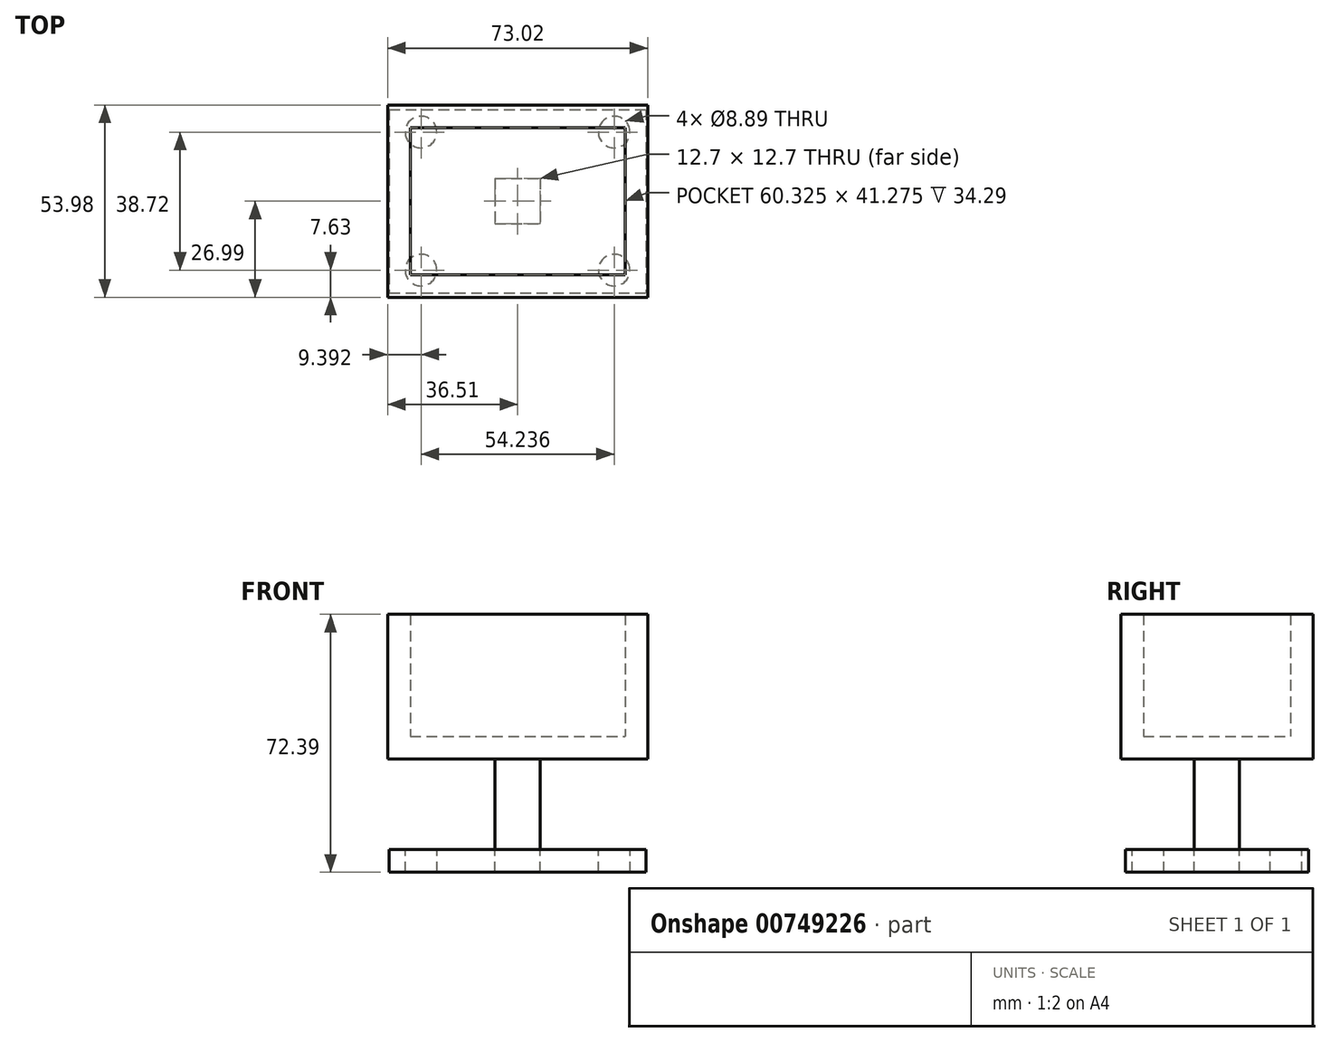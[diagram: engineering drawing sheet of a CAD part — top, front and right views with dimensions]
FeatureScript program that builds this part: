
annotation { "Feature Type Name" : "Feature", "Feature Type Description" : "" }
export const myFeature = defineFeature(function(context is Context, id is Id, definition is map)
    precondition{}
    {
        {
            var Q0;
            Q0=qCreatedBy(makeId("Top.planeOp"),FACE);
            var sketch = newSketch(context, id + "F0", { "sketchPlane" : qUnion([Q0])});
            skLineSegment(sketch, "E0.bottom", {"start": v(-30.16, -20.64) * mm, "end": v(30.16, -20.64) * mm});
            skLineSegment(sketch, "E0.top", {"start": v(-30.16, 20.64) * mm, "end": v(30.16, 20.64) * mm});
            skLineSegment(sketch, "E0.left", {"start": v(-30.16, -20.64) * mm, "end": v(-30.16, 20.64) * mm});
            skLineSegment(sketch, "E0.right", {"start": v(30.16, -20.64) * mm, "end": v(30.16, 20.64) * mm});
            skPoint(sketch, "E0.middle", {"position": v(0, 0) * mm});
            skSolve(sketch);
        }
        {
            var Q0;
            Q0=makeQuery(id+"F0.imprint","IMPRINT",FACE,{"disambiguationData":[TD([[makeQuery(id+"F0.imprint","IMPRINT",EDGE,{"derivedFrom":sQuery(id+"F0.wireOp",EDGE,"E0.bottom")}),1.0]])]});
            extrude(context, id + "F1", {"entities" : qUnion([Q0]), "depth" : 6.35 * mm});
        }
        {
            var Q0;
            Q0=makeQuery(id+"F1.opExtrude","CAP_FACE",FACE,{"disambiguationData":[OSD([sQuery(id+"F0.wireOp",EDGE,"E0.bottom"),sQuery(id+"F0.wireOp",EDGE,"E0.top"),sQuery(id+"F0.wireOp",EDGE,"E0.left"),sQuery(id+"F0.wireOp",EDGE,"E0.right")])],"isStart":true});
            var sketch = newSketch(context, id + "F2", { "sketchPlane" : qUnion([Q0])});
            skLineSegment(sketch, "E1.bottom", {"start": v(-6.35, -6.35) * mm, "end": v(6.35, -6.35) * mm});
            skLineSegment(sketch, "E1.top", {"start": v(-6.35, 6.35) * mm, "end": v(6.35, 6.35) * mm});
            skLineSegment(sketch, "E1.left", {"start": v(-6.35, -6.35) * mm, "end": v(-6.35, 6.35) * mm});
            skLineSegment(sketch, "E1.right", {"start": v(6.35, -6.35) * mm, "end": v(6.35, 6.35) * mm});
            skPoint(sketch, "E1.middle", {"position": v(0, 0) * mm});
            skSolve(sketch);
        }
        {
            var Q0;
            Q0=makeQuery(id+"F2.imprint","IMPRINT",FACE,{"disambiguationData":[TD([[makeQuery(id+"F2.imprint","IMPRINT",EDGE,{"derivedFrom":sQuery(id+"F2.wireOp",EDGE,"E1.bottom")}),1.0]])]});
            extrude(context, id + "F3", {"entities" : qUnion([Q0]), "operationType" : NewBodyOperationType.ADD, "depth" : 25.4 * mm});
        }
        {
            var Q0;
            Q0=makeQuery(id+"F3.opExtrude","CAP_FACE",FACE,{"disambiguationData":[OSD([sQuery(id+"F2.wireOp",EDGE,"E1.bottom"),sQuery(id+"F2.wireOp",EDGE,"E1.top"),sQuery(id+"F2.wireOp",EDGE,"E1.left"),sQuery(id+"F2.wireOp",EDGE,"E1.right")])],"isStart":false});
            var sketch = newSketch(context, id + "F4", { "sketchPlane" : qUnion([Q0])});
            skLineSegment(sketch, "E2.bottom", {"start": v(-36, -25.7) * mm, "end": v(36, -25.7) * mm});
            skLineSegment(sketch, "E2.top", {"start": v(-36, 25.7) * mm, "end": v(36, 25.7) * mm});
            skLineSegment(sketch, "E2.left", {"start": v(-36, -25.7) * mm, "end": v(-36, 25.7) * mm});
            skLineSegment(sketch, "E2.right", {"start": v(36, -25.7) * mm, "end": v(36, 25.7) * mm});
            skPoint(sketch, "E2.middle", {"position": v(0, 0) * mm});
            skLineSegment(sketch, "E3", {"start": v(-36, 25.7) * mm, "end": v(0, 0) * mm});
            skLineSegment(sketch, "E4", {"start": v(0, 0) * mm, "end": v(-36, -25.7) * mm});
            skLineSegment(sketch, "E5", {"start": v(0, 0) * mm, "end": v(36, 25.7) * mm});
            skLineSegment(sketch, "E6", {"start": v(0, 0) * mm, "end": v(36, -25.7) * mm});
            skCircle(sketch, "E7", {"center": v(-27.12, 19.36) * mm, "radius": 4.45 * mm});
            skCircle(sketch, "E8", {"center": v(-27.12, -19.36) * mm, "radius": 4.45 * mm});
            skCircle(sketch, "E9", {"center": v(27.12, -19.36) * mm, "radius": 4.45 * mm});
            skCircle(sketch, "E10", {"center": v(27.12, 19.36) * mm, "radius": 4.45 * mm});
            skSolve(sketch);
        }
        {
            var Q0;
            {var subQ10=sQuery(id+"F4.wireOp",EDGE,"E2.left");Q0=makeQuery(id+"F4.imprint","IMPRINT",FACE,{"disambiguationData":[TD([[makeQuery(id+"F4.imprint","IMPRINT",EDGE,{"derivedFrom":subQ10}),-1.0]])]});}
            var Q1;
            {var subQ6=sQuery(id+"F4.wireOp",EDGE,"E2.top");Q1=makeQuery(id+"F4.imprint","IMPRINT",FACE,{"disambiguationData":[TD([[makeQuery(id+"F4.imprint","IMPRINT",EDGE,{"derivedFrom":subQ6}),-1.0]])]});}
            var Q2;
            {var subQ6=sQuery(id+"F4.wireOp",EDGE,"E2.right");Q2=makeQuery(id+"F4.imprint","IMPRINT",FACE,{"disambiguationData":[TD([[makeQuery(id+"F4.imprint","IMPRINT",EDGE,{"derivedFrom":subQ6}),1.0]])]});}
            var Q3;
            {var subQ7=sQuery(id+"F4.wireOp",EDGE,"E2.bottom");Q3=makeQuery(id+"F4.imprint","IMPRINT",FACE,{"disambiguationData":[TD([[makeQuery(id+"F4.imprint","IMPRINT",EDGE,{"derivedFrom":subQ7}),1.0]])]});}
            extrude(context, id + "F5", {"entities" : qUnion([Q0, Q1, Q2, Q3]), "depth" : 6.35 * mm});
        }
        {
            var Q0;
            Q0=makeQuery(id+"F1.opExtrude","CAP_FACE",FACE,{"disambiguationData":[OSD([sQuery(id+"F0.wireOp",EDGE,"E0.bottom"),sQuery(id+"F0.wireOp",EDGE,"E0.top"),sQuery(id+"F0.wireOp",EDGE,"E0.left"),sQuery(id+"F0.wireOp",EDGE,"E0.right")])],"isStart":true});
            var sketch = newSketch(context, id + "F6", { "sketchPlane" : qUnion([Q0])});
            skLineSegment(sketch, "E11.bottom", {"start": v(-30.16, 20.64) * mm, "end": v(-30.16, 20.64) * mm});
            skLineSegment(sketch, "E11.top", {"start": v(-30.16, -20.64) * mm, "end": v(-30.16, -20.64) * mm});
            skLineSegment(sketch, "E11.left", {"start": v(-30.16, 20.64) * mm, "end": v(-30.16, -20.64) * mm});
            skLineSegment(sketch, "E11.right", {"start": v(-30.16, 20.64) * mm, "end": v(-30.16, -20.64) * mm});
            skLineSegment(sketch, "E12", {"start": v(-36.51, -20.64) * mm, "end": v(-36.51, 20.64) * mm});
            skLineSegment(sketch, "E13", {"start": v(-36.51, 20.64) * mm, "end": v(-30.16, 20.64) * mm});
            skLineSegment(sketch, "E14", {"start": v(30.16, 20.64) * mm, "end": v(30.16, -20.64) * mm});
            skLineSegment(sketch, "E15", {"start": v(30.16, -20.64) * mm, "end": v(36.51, -20.64) * mm});
            skLineSegment(sketch, "E16", {"start": v(36.51, -20.64) * mm, "end": v(36.51, 20.64) * mm});
            skLineSegment(sketch, "E17", {"start": v(36.51, 20.64) * mm, "end": v(30.16, 20.64) * mm});
            skLineSegment(sketch, "E18.bottom", {"start": v(36.51, -20.64) * mm, "end": v(-36.51, -20.64) * mm});
            skLineSegment(sketch, "E18.top", {"start": v(36.51, -26.99) * mm, "end": v(-36.51, -26.99) * mm});
            skLineSegment(sketch, "E18.left", {"start": v(36.51, -20.64) * mm, "end": v(36.51, -26.99) * mm});
            skLineSegment(sketch, "E18.right", {"start": v(-36.51, -20.64) * mm, "end": v(-36.51, -26.99) * mm});
            skLineSegment(sketch, "E19.bottom", {"start": v(36.51, 20.64) * mm, "end": v(-36.51, 20.64) * mm});
            skLineSegment(sketch, "E19.top", {"start": v(36.51, 26.99) * mm, "end": v(-36.51, 26.99) * mm});
            skLineSegment(sketch, "E19.left", {"start": v(36.51, 20.64) * mm, "end": v(36.51, 26.99) * mm});
            skLineSegment(sketch, "E19.right", {"start": v(-36.51, 20.64) * mm, "end": v(-36.51, 26.99) * mm});
            skSolve(sketch);
        }
        {
            var Q0;
            Q0=qSketchRegion(id+"F6",true);
            extrude(context, id + "F7", {"entities" : qUnion([Q0]), "operationType" : NewBodyOperationType.ADD, "oppositeDirection" : true, "depth" : 40.64 * mm});
        }
    });
